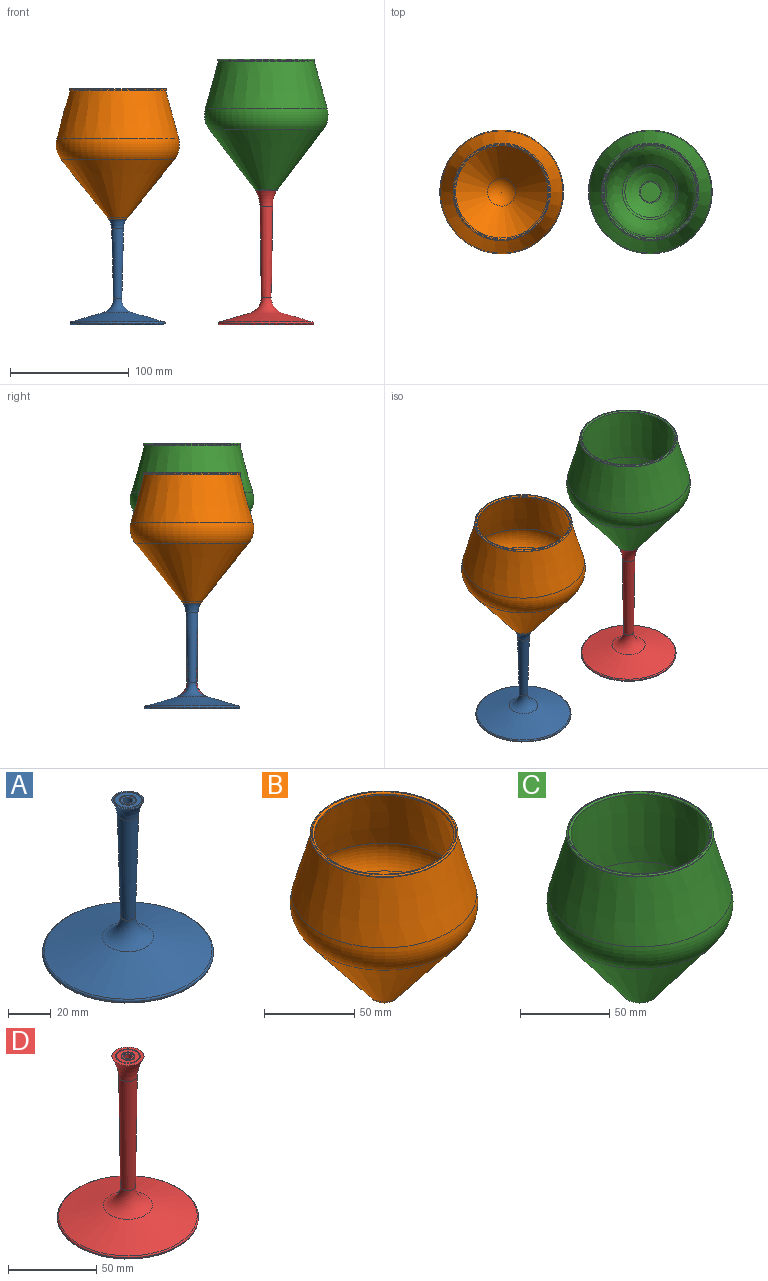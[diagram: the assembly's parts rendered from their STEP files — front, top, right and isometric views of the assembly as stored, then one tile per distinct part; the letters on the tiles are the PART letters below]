
ASSEMBLY  parts=4 mates=3
PART A: 21 faces, bbox 86.6x86.6x90.7 mm
  f0: torus R=19.96mm, axis (0,0,-1), area 311.7mm2, adj f1,f6
  f1: plane 15x15mm, normal (0,0,1), area 35.6mm2, adj f0,f18
  f2: plane 12.6x12.6mm, normal (0,0,1), area 75.5mm2, adj f17,f20
  f3: plane 7.1x7.1mm, normal (0,0,1), area 22.9mm2, adj f4,f19
  f4: cylinder r=2.3mm len=4.6mm, axis (0,0,1), area 57.8mm2, adj f3,f5
  f5: plane 4.6x4.6mm, normal (0,0,1), area 16.6mm2, adj f4
  f6: cone r=4.23mm half-angle=1.5deg, axis (0,0,1), area 1550.9mm2, adj f0,f7
  f7: torus R=15.48mm, axis (0,0,-1), area 638.4mm2, adj f6,f8
  f8: cone r=25.69mm half-angle=73.6deg, axis (0,0,-1), area 4573.5mm2, adj f7,f9
  f9: torus R=39mm, axis (0,0,-1), area 320.9mm2, adj f8,f10
  f10: cylinder r=40mm len=80mm, axis (0,0,-1), area 63.2mm2, adj f9,f11
  f11: torus R=39mm, axis (0,0,-1), area 391.2mm2, adj f10,f12
  f12: plane 78x78mm, normal (0,0,-1), area 465.4mm2, adj f11,f13
  f13: cone r=23.38mm half-angle=73.6deg, axis (0,0,-1), area 4186.3mm2, adj f12,f14,f15
  f14: torus R=3mm, axis (0,0,-1), area 136.5mm2, adj f13,f15,f16
  f15: torus R=3mm, axis (0,0,-1), area 136.5mm2, adj f13,f14,f16
  f16: plane 6x6mm, normal (0,0,-1), area 28.3mm2, adj f14,f15
  f17: cone r=6.4mm half-angle=30deg, axis (0,0,1), area 16.2mm2, adj f2,f18
  f18: cone r=6.6mm half-angle=30deg, axis (0,0,-1), area 16.8mm2, adj f1,f17
  f19: cone r=3.65mm half-angle=30deg, axis (0,0,1), area 9.3mm2, adj f3,f20
  f20: cone r=3.85mm half-angle=30deg, axis (0,0,-1), area 9.8mm2, adj f2,f19
PART B: 18 faces, bbox 112.6x112.6x117.8 mm
  f0: cone r=40.27mm half-angle=36.7deg, axis (0,0,-1), area 53.6mm2, adj f1,f17
  f1: cone r=40.27mm half-angle=15.4deg, axis (0,0,-1), area 11955.3mm2, adj f0,f2
  f2: torus R=32mm, axis (0,0,1), area 6017.9mm2, adj f1,f3
  f3: cone r=8.56mm half-angle=38.6deg, axis (0,0,1), area 11067.8mm2, adj f2,f4
  f4: torus R=20.29mm, axis (0,0,1), area 93.5mm2, adj f3,f5
  f5: plane 15x15mm, normal (0,0,-1), area 159.4mm2, adj f4,f6
  f6: cone r=2mm half-angle=5deg, axis (0,0,1), area 54.9mm2, adj f5,f7
  f7: plane 4x4mm, normal (0,0,-1), area 12.6mm2, adj f6
  f8: sphere r=15mm, area 532.5mm2, adj f9
  f9: cone r=46.47mm half-angle=38.6deg, axis (0,0,1), area 10187.8mm2, adj f8,f10
  f10: torus R=32mm, axis (0,0,1), area 5411.7mm2, adj f9,f11
  f11: cone r=38.76mm half-angle=15.4deg, axis (0,0,-1), area 11631.8mm2, adj f10,f12
  f12: cylinder r=38.76mm len=77.53mm, axis (0,0,1), area 195.5mm2, adj f11,f13
  f13: torus R=39.76mm, axis (0,0,1), area 386.2mm2, adj f12,f14
  f14: plane 80.47x80.47mm, normal (0,0,1), area 119mm2, adj f13,f15
  f15: torus R=40.24mm, axis (0,0,1), area 301.4mm2, adj f14,f16
  f16: torus R=40.29mm, axis (0,0,1), area 281.4mm2, adj f15,f17
  f17: plane 80.57x80.57mm, normal (0,0,-1), area 36.6mm2, adj f0,f16
PART C: 33 faces, bbox 112.6x112.6x114 mm
  f0: torus R=40.29mm, axis (0,0,-1), area 281.4mm2, adj f1,f4
  f1: torus R=40.24mm, axis (0,0,-1), area 301.4mm2, adj f0,f2
  f2: plane 80.47x80.47mm, normal (0,0,1), area 119mm2, adj f1,f11
  f3: cone r=40.27mm half-angle=36.7deg, axis (0,0,-1), area 53.6mm2, adj f4,f18
  f4: plane 80.57x80.57mm, normal (0,0,-1), area 36.6mm2, adj f0,f3
  f5: plane 17.03x17.03mm, normal (0,0,1), area 227.7mm2, adj f6
  f6: torus R=8.51mm, axis (0,0,1), area 40.5mm2, adj f5,f7
  f7: revolved ~42.79x42.79mm, area 1460.5mm2, adj f6,f8
  f8: torus R=2.98mm, axis (0,0,1), area 443.1mm2, adj f7,f9
  f9: revolved ~74.68x74.68mm, area 9139.7mm2, adj f8,f10
  f10: cone r=38.76mm half-angle=1.8deg, axis (0,0,1), area 10831.3mm2, adj f9,f11
  f11: torus R=39.76mm, axis (0,0,1), area 388.3mm2, adj f2,f10
  f12: plane 4x4mm, normal (0,0,-1), area 12.6mm2, adj f13
  f13: cone r=2mm half-angle=5deg, axis (0,0,1), area 54.9mm2, adj f12,f14
  f14: plane 18.27x18.27mm, normal (0,0,-1), area 244.8mm2, adj f13,f15
  f15: torus R=10.86mm, axis (0,0,-1), area 13.7mm2, adj f14,f16
  f16: cone r=47.9mm half-angle=37.3deg, axis (0,0,1), area 11445.9mm2, adj f15,f17
  f17: torus R=32mm, axis (0,0,-1), area 5888mm2, adj f16,f18
  f18: cone r=40.27mm half-angle=15.4deg, axis (0,0,-1), area 11955.3mm2, adj f3,f17
  f19: revolved ~77.42x77.42mm, area 8138.7mm2, adj f20,f21
  f20: cone r=40.27mm half-angle=2deg, axis (0,0,1), area 9800.9mm2, adj f19,f23
  f21: cone r=10.58mm half-angle=37.3deg, axis (0,0,1), area 6916.7mm2, adj f19,f22
  f22: torus R=32mm, axis (0,0,-1), area 5294.5mm2, adj f21,f23
  f23: cone r=38.76mm half-angle=15.4deg, axis (0,0,-1), area 10388.6mm2, adj f20,f22
  f24: plane 4x4mm, normal (0,0,-1), area 12.6mm2, adj f25
  f25: cone r=2mm half-angle=8deg, axis (0,0,1), area 45.8mm2, adj f24,f26
  f26: plane 13.92x13.92mm, normal (0,0,-1), area 133.2mm2, adj f25,f27
  f27: torus R=6.96mm, axis (0,0,1), area 153.4mm2, adj f26,f28
  f28: torus R=14.41mm, axis (0,0,1), area 213.9mm2, adj f27,f29
  f29: revolved ~37.85x37.85mm, area 819.4mm2, adj f28,f32
  f30: sphere r=40mm, area 180.8mm2, adj f31
  f31: torus R=6.61mm, axis (0,0,-1), area 210.4mm2, adj f30,f32
  f32: cone r=10.58mm half-angle=37.3deg, axis (0,0,1), area 1275.1mm2, adj f29,f31
PART D: 21 faces, bbox 86.6x86.6x118.6 mm
  f0: torus R=33.25mm, axis (0,0,-1), area 602.9mm2, adj f1,f6
  f1: plane 18.27x18.27mm, normal (0,0,1), area 110.3mm2, adj f0,f20
  f2: plane 7.1x7.1mm, normal (0,0,1), area 22.9mm2, adj f4,f17
  f3: plane 13.1x13.1mm, normal (0,0,1), area 85.6mm2, adj f18,f19
  f4: cylinder r=2.3mm len=4.6mm, axis (0,0,1), area 57.8mm2, adj f2,f5
  f5: plane 4.6x4.6mm, normal (0,0,1), area 16.6mm2, adj f4
  f6: cone r=4.75mm half-angle=0.8deg, axis (0,0,1), area 2278.8mm2, adj f0,f7
  f7: torus R=17.75mm, axis (0,0,-1), area 840.6mm2, adj f6,f8
  f8: cone r=26.61mm half-angle=73.6deg, axis (0,0,-1), area 4416.2mm2, adj f7,f9
  f9: torus R=39mm, axis (0,0,-1), area 320.9mm2, adj f8,f10
  f10: cylinder r=40mm len=80mm, axis (0,0,-1), area 63.2mm2, adj f9,f11
  f11: torus R=39mm, axis (0,0,-1), area 391.2mm2, adj f10,f12
  f12: plane 78x78mm, normal (0,0,-1), area 465.4mm2, adj f11,f13
  f13: cone r=23.38mm half-angle=73.6deg, axis (0,0,-1), area 4186.3mm2, adj f12,f14,f15
  f14: torus R=3mm, axis (0,0,-1), area 136.5mm2, adj f13,f15,f16
  f15: torus R=3mm, axis (0,0,-1), area 136.5mm2, adj f13,f14,f16
  f16: plane 6x6mm, normal (0,0,-1), area 28.3mm2, adj f14,f15
  f17: cone r=3.65mm half-angle=30deg, axis (0,0,1), area 9.3mm2, adj f2,f18
  f18: cone r=3.85mm half-angle=30deg, axis (0,0,-1), area 9.8mm2, adj f3,f17
  f19: cone r=6.65mm half-angle=30deg, axis (0,0,1), area 16.9mm2, adj f3,f20
  f20: cone r=6.85mm half-angle=30deg, axis (0,0,-1), area 17.4mm2, adj f1,f19
PLACE A t=(-200,0,-214)mm
PLACE B t=(-200,0,-24.65)mm
PLACE C t=(-75,0,0)mm
PLACE D t=(-75,0,-434)mm
MATE fastened D.f4 <-> C.f0  axis (0,0,1) through (-75,0,-110)mm
MATE fastened B.f4 <-> A.f0  axis (0,0,-1) through (-200,0,-134.65)mm
MATE fastened D.f11 <-> A.f16  axis (0,0,-1) through (-75,0,-214)mm
